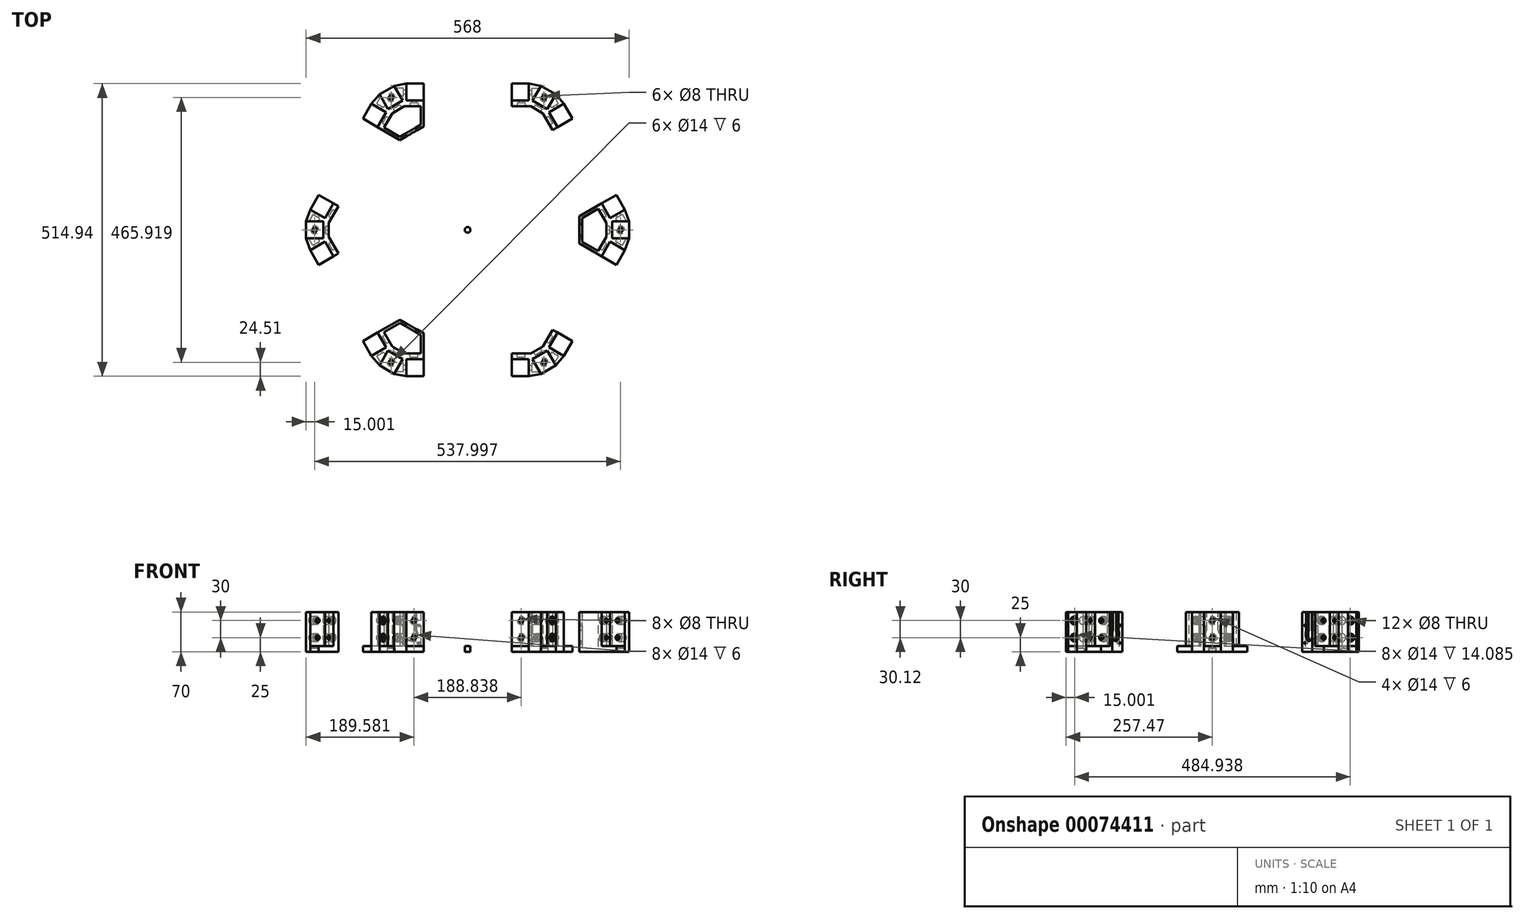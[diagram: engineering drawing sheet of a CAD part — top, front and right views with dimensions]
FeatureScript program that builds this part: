
annotation { "Feature Type Name" : "Feature", "Feature Type Description" : "" }
export const myFeature = defineFeature(function(context is Context, id is Id, definition is map)
    precondition{}
    {
        {
            var Q0;
            Q0=qCreatedBy(makeId("Top.planeOp"),FACE);
            var sketch = newSketch(context, id + "F0", { "sketchPlane" : qUnion([Q0])});
            skCircle(sketch, "E0", {"center": v(0, 0) * mm, "radius": 150 * mm, "construction": true});
            skCircle(sketch, "E1.cCircle", {"center": v(0, 0) * mm, "radius": 253.45 * mm, "construction": true});
            skLineSegment(sketch, "E1.0", {"start": v(-146.33, 253.45) * mm, "end": v(146.33, 253.45) * mm, "construction": true});
            skLineSegment(sketch, "E1.1", {"start": v(146.33, 253.45) * mm, "end": v(292.66, 0) * mm, "construction": true});
            skLineSegment(sketch, "E1.2", {"start": v(292.66, 0) * mm, "end": v(146.33, -253.45) * mm, "construction": true});
            skLineSegment(sketch, "E1.3", {"start": v(146.33, -253.45) * mm, "end": v(-146.33, -253.45) * mm, "construction": true});
            skLineSegment(sketch, "E1.4", {"start": v(-146.33, -253.45) * mm, "end": v(-292.66, 0) * mm, "construction": true});
            skLineSegment(sketch, "E1.5", {"start": v(-292.66, 0) * mm, "end": v(-146.33, 253.45) * mm, "construction": true});
            skPoint(sketch, "E1.0.midPoint", {"position": v(0, 253.45) * mm});
            skLineSegment(sketch, "E2", {"start": v(146.33, 253.45) * mm, "end": v(-146.33, -253.45) * mm, "construction": true});
            skCircle(sketch, "E3.cCircle", {"center": v(0, 0) * mm, "radius": 284 * mm, "construction": true});
            skLineSegment(sketch, "E3.0", {"start": v(0, 327.93) * mm, "end": v(284, 163.97) * mm, "construction": true});
            skLineSegment(sketch, "E3.1", {"start": v(284, 163.97) * mm, "end": v(284, -163.97) * mm, "construction": true});
            skLineSegment(sketch, "E3.2", {"start": v(284, -163.97) * mm, "end": v(0, -327.93) * mm, "construction": true});
            skLineSegment(sketch, "E3.3", {"start": v(0, -327.93) * mm, "end": v(-284, -163.97) * mm, "construction": true});
            skLineSegment(sketch, "E3.4", {"start": v(-284, -163.97) * mm, "end": v(-284, 163.97) * mm, "construction": true});
            skLineSegment(sketch, "E3.5", {"start": v(-284, 163.97) * mm, "end": v(0, 327.93) * mm, "construction": true});
            skPoint(sketch, "E3.0.midPoint", {"position": v(142, 245.95) * mm});
            skLineSegment(sketch, "E4", {"start": v(154.99, 238.45) * mm, "end": v(129, 253.45) * mm});
            skLineSegment(sketch, "E5", {"start": v(-154.99, 238.45) * mm, "end": v(-129, 253.45) * mm});
            skLineSegment(sketch, "E6", {"start": v(-129, 253.45) * mm, "end": v(-114, 227.47) * mm});
            skLineSegment(sketch, "E7", {"start": v(-114, 227.47) * mm, "end": v(-139.99, 212.47) * mm});
            skLineSegment(sketch, "E8", {"start": v(-139.99, 212.47) * mm, "end": v(-154.99, 238.45) * mm});
            skLineSegment(sketch, "E9", {"start": v(129, 253.45) * mm, "end": v(114, 227.47) * mm});
            skLineSegment(sketch, "E10", {"start": v(114, 227.47) * mm, "end": v(139.99, 212.47) * mm});
            skLineSegment(sketch, "E11", {"start": v(139.99, 212.47) * mm, "end": v(154.99, 238.45) * mm});
            skLineSegment(sketch, "E12", {"start": v(284, 15) * mm, "end": v(284, -15) * mm});
            skLineSegment(sketch, "E13", {"start": v(284, -15) * mm, "end": v(254, -15) * mm});
            skLineSegment(sketch, "E14", {"start": v(254, -15) * mm, "end": v(254, 15) * mm});
            skLineSegment(sketch, "E15", {"start": v(254, 15) * mm, "end": v(284, 15) * mm});
            skLineSegment(sketch, "E16", {"start": v(154.99, -238.45) * mm, "end": v(129, -253.45) * mm});
            skLineSegment(sketch, "E17", {"start": v(129, -253.45) * mm, "end": v(114, -227.47) * mm});
            skLineSegment(sketch, "E18", {"start": v(114, -227.47) * mm, "end": v(139.99, -212.47) * mm});
            skLineSegment(sketch, "E19", {"start": v(139.99, -212.47) * mm, "end": v(154.99, -238.45) * mm});
            skLineSegment(sketch, "E20", {"start": v(-129, -253.45) * mm, "end": v(-154.99, -238.45) * mm});
            skLineSegment(sketch, "E21", {"start": v(-154.99, -238.45) * mm, "end": v(-139.99, -212.47) * mm});
            skLineSegment(sketch, "E22", {"start": v(-139.99, -212.47) * mm, "end": v(-114, -227.47) * mm});
            skLineSegment(sketch, "E23", {"start": v(-114, -227.47) * mm, "end": v(-129, -253.45) * mm});
            skLineSegment(sketch, "E24", {"start": v(-284, -15) * mm, "end": v(-284, 15) * mm});
            skLineSegment(sketch, "E25", {"start": v(-284, 15) * mm, "end": v(-254, 15) * mm});
            skLineSegment(sketch, "E26", {"start": v(-254, 15) * mm, "end": v(-254, -15) * mm});
            skLineSegment(sketch, "E27", {"start": v(-254, -15) * mm, "end": v(-284, -15) * mm});
            skLineSegment(sketch, "E28", {"start": v(-254, 15) * mm, "end": v(-139.99, 212.47) * mm, "construction": true});
            skLineSegment(sketch, "E29", {"start": v(-254, -15) * mm, "end": v(-139.99, -212.47) * mm, "construction": true});
            skLineSegment(sketch, "E30", {"start": v(-114, -227.47) * mm, "end": v(114, -227.47) * mm, "construction": true});
            skLineSegment(sketch, "E31", {"start": v(139.99, -212.47) * mm, "end": v(254, -15) * mm, "construction": true});
            skLineSegment(sketch, "E32", {"start": v(254, 15) * mm, "end": v(139.99, 212.47) * mm, "construction": true});
            skLineSegment(sketch, "E33", {"start": v(114, 227.47) * mm, "end": v(-114, 227.47) * mm, "construction": true});
            skLineSegment(sketch, "E34", {"start": v(-114, 227.47) * mm, "end": v(-107.5, 227.47) * mm, "construction": true});
            skLineSegment(sketch, "E35", {"start": v(-107.5, 227.47) * mm, "end": v(-77.5, 227.47) * mm});
            skLineSegment(sketch, "E36", {"start": v(-77.5, 227.47) * mm, "end": v(-77.5, 217.47) * mm});
            skLineSegment(sketch, "E37", {"start": v(-77.5, 217.47) * mm, "end": v(-111.33, 217.47) * mm});
            skLineSegment(sketch, "E38", {"start": v(-111.33, 217.47) * mm, "end": v(-132.67, 205.15) * mm});
            skLineSegment(sketch, "E39", {"start": v(-132.67, 205.15) * mm, "end": v(-149.58, 175.86) * mm});
            skLineSegment(sketch, "E40", {"start": v(-149.58, 175.86) * mm, "end": v(-158.24, 180.86) * mm});
            skLineSegment(sketch, "E41", {"start": v(-158.24, 180.86) * mm, "end": v(-143.24, 206.84) * mm});
            skLineSegment(sketch, "E42", {"start": v(-143.24, 206.84) * mm, "end": v(-139.99, 212.47) * mm, "construction": true});
            skLineSegment(sketch, "E43", {"start": v(-154.99, 238.45) * mm, "end": v(-114, 227.47) * mm, "construction": true});
            skLineSegment(sketch, "E44", {"start": v(-129, 253.45) * mm, "end": v(-139.99, 212.47) * mm, "construction": true});
            skPoint(sketch, "E45", {"position": v(-134.5, 232.96) * mm});
            skCircle(sketch, "E46", {"center": v(0, 0) * mm, "radius": 5 * mm});
            skLineSegment(sketch, "E47", {"start": v(-118.15, 234.63) * mm, "end": v(-118.15, 248.63) * mm, "construction": true});
            skLineSegment(sketch, "E48.0", {"start": v(-112.15, 234.63) * mm, "end": v(-112.15, 248.63) * mm, "construction": true});
            skLineSegment(sketch, "E49.0", {"start": v(-107.5, 257.47) * mm, "end": v(-77.5, 257.47) * mm});
            skLineSegment(sketch, "E50.0", {"start": v(-184.22, 195.86) * mm, "end": v(-169.22, 221.84) * mm});
            skLineSegment(sketch, "E51", {"start": v(-154.99, 238.45) * mm, "end": v(-169.22, 221.84) * mm});
            skLineSegment(sketch, "E52", {"start": v(-107.5, 257.47) * mm, "end": v(-129, 253.45) * mm});
            skLineSegment(sketch, "E53", {"start": v(-107.5, 227.47) * mm, "end": v(-107.5, 257.47) * mm});
            skLineSegment(sketch, "E54", {"start": v(-77.5, 257.47) * mm, "end": v(-77.5, 227.47) * mm});
            skLineSegment(sketch, "E55", {"start": v(-158.24, 180.86) * mm, "end": v(-184.22, 195.86) * mm});
            skLineSegment(sketch, "E56", {"start": v(-143.24, 206.84) * mm, "end": v(-169.22, 221.84) * mm});
            skLineSegment(sketch, "E57", {"start": v(-107.5, 242.47) * mm, "end": v(-122.67, 242.47) * mm, "construction": true});
            skLineSegment(sketch, "E58", {"start": v(-149.58, 175.86) * mm, "end": v(-118.88, 158.14) * mm});
            skLineSegment(sketch, "E59", {"start": v(-118.88, 158.14) * mm, "end": v(-77.5, 182.02) * mm});
            skLineSegment(sketch, "E60", {"start": v(-77.5, 182.02) * mm, "end": v(-77.5, 217.47) * mm});
            skLineSegment(sketch, "E61", {"start": v(-122, 211.3) * mm, "end": v(-98.2, 170.08) * mm, "construction": true});
            skLineSegment(sketch, "E62.1", {"start": v(-118.88, 163.9) * mm, "end": v(-82.5, 184.9) * mm});
            skLineSegment(sketch, "E62.2", {"start": v(-147.08, 180.19) * mm, "end": v(-118.88, 163.9) * mm});
            skLineSegment(sketch, "E63", {"start": v(-82.5, 184.9) * mm, "end": v(-82.5, 217.47) * mm});
            skSolve(sketch);
        }
        {
            var Q0;
            Q0=makeQuery(id+"F0.imprint","IMPRINT",FACE,{"disambiguationData":[TD([[makeQuery(id+"F0.imprint","IMPRINT",EDGE,{"derivedFrom":sQuery(id+"F0.wireOp",EDGE,"E6")}),1.0]])]});
            var Q1;
            Q1=makeQuery(id+"F0.imprint","IMPRINT",FACE,{"disambiguationData":[TD([[makeQuery(id+"F0.imprint","IMPRINT",EDGE,{"derivedFrom":sQuery(id+"F0.wireOp",EDGE,"E25")}),1.0]])]});
            extrude(context, id + "F1", {"entities" : qUnion([Q0, Q1]), "depth" : 70 * mm});
        }
        {
            var Q0;
            Q0=makeQuery(id+"F0.imprint","IMPRINT",FACE,{"disambiguationData":[TD([[makeQuery(id+"F0.imprint","IMPRINT",EDGE,{"derivedFrom":sQuery(id+"F0.wireOp",EDGE,"gfhvg1Dc-7iLy-Ra7s-P4iO-IVNU9nK08UEl")}),-1.0]])]});
            var Q1;
            Q1=makeQuery(id+"F0.imprint","IMPRINT",FACE,{"disambiguationData":[TD([[makeQuery(id+"F0.imprint","IMPRINT",EDGE,{"derivedFrom":sQuery(id+"F0.wireOp",EDGE,"E5")}),-1.0]])]});
            var Q2;
            Q2=makeQuery(id+"F0.imprint","IMPRINT",FACE,{"disambiguationData":[TD([[makeQuery(id+"F0.imprint","IMPRINT",EDGE,{"derivedFrom":sQuery(id+"F0.wireOp",EDGE,"E41")}),1.0]])]});
            var Q3;
            Q3=makeQuery(id+"F0.imprint","IMPRINT",FACE,{"disambiguationData":[TD([[makeQuery(id+"F0.imprint","IMPRINT",EDGE,{"derivedFrom":sQuery(id+"F0.wireOp",EDGE,"kg992uxK-LLUE-ufWO-S31q-0ohrqG9XmHnS")}),1.0]])]});
            var Q4;
            Q4=makeQuery(id+"F0.imprint","IMPRINT",FACE,{"disambiguationData":[TD([[makeQuery(id+"F0.imprint","IMPRINT",EDGE,{"derivedFrom":sQuery(id+"F0.wireOp",EDGE,"zyB05oXD-GM3K-m8Ih-r1cb-nkl0ugIBj9Wl")}),1.0]])]});
            var Q5;
            Q5=makeQuery(id+"F0.imprint","IMPRINT",FACE,{"disambiguationData":[TD([[makeQuery(id+"F0.imprint","IMPRINT",EDGE,{"derivedFrom":sQuery(id+"F0.wireOp",EDGE,"ZcA5kg2R-B5n5-RwAf-hmlT-K68Li3uCES3B")}),-1.0]])]});
            var Q6;
            Q6=makeQuery(id+"F0.imprint","IMPRINT",FACE,{"disambiguationData":[TD([[makeQuery(id+"F0.imprint","IMPRINT",EDGE,{"derivedFrom":sQuery(id+"F0.wireOp",EDGE,"E46")}),1.0]])]});
            var Q7;
            Q7=makeQuery(id+"F0.imprint","IMPRINT",FACE,{"disambiguationData":[TD([[makeQuery(id+"F0.imprint","IMPRINT",EDGE,{"derivedFrom":sQuery(id+"F0.wireOp",EDGE,"E35")}),1.0]])]});
            extrude(context, id + "F2", {"entities" : qUnion([Q0, Q1, Q2, Q3, Q4, Q5, Q6, Q7]), "operationType" : NewBodyOperationType.ADD, "depth" : 10 * mm});
        }
        {
            var Q0;
            Q0=makeQuery(id+"F1.opExtrude","SWEPT_FACE",FACE,{"disambiguationData":[OSD([sQuery(id+"F0.wireOp",EDGE,"E53")])]});
            var Q1;
            Q1=makeQuery(id+"F1.opExtrude","CAP_VERTEX",VERTEX,{"disambiguationData":[OSD([sQuery(id+"F0.wireOp",EDGE,"E5"),sQuery(id+"F0.wireOp",EDGE,"E6"),sQuery(id+"F0.wireOp",EDGE,"E52")])],"isStart":false});
            cPlane(context, id + "F3", {"entities" : qUnion([Q0, Q1]), "cplaneType" : CPlaneType.PLANE_POINT, "offset" : 150 * mm, "width" : 150 * mm, "height" : 150 * mm});
        }
        {
            var Q0;
            Q0=qCreatedBy(id+"F3.planeOp",FACE);
            var sketch = newSketch(context, id + "F4", { "sketchPlane" : qUnion([Q0])});
            skLineSegment(sketch, "E64.0", {"start": v(242.47, 70.12) * mm, "end": v(242.47, 10) * mm, "construction": true});
            skPoint(sketch, "E65", {"position": v(242.47, 55.12) * mm});
            skPoint(sketch, "E66", {"position": v(242.47, 25) * mm});
            skSolve(sketch);
        }
        {
            var Q0;
            Q0=makeQuery(id+"F1.opExtrude","SWEPT_FACE",FACE,{"disambiguationData":[OSD([sQuery(id+"F0.wireOp",EDGE,"E56")])]});
            var Q1;
            Q1=makeQuery(id+"F1.opExtrude","CAP_VERTEX",VERTEX,{"disambiguationData":[OSD([sQuery(id+"F0.wireOp",EDGE,"E5"),sQuery(id+"F0.wireOp",EDGE,"E8"),sQuery(id+"F0.wireOp",EDGE,"E51")])],"isStart":false});
            cPlane(context, id + "F5", {"entities" : qUnion([Q0, Q1]), "cplaneType" : CPlaneType.PLANE_POINT, "offset" : 150 * mm, "width" : 150 * mm, "height" : 150 * mm});
        }
        {
            var Q0;
            Q0=qCreatedBy(id+"F5.planeOp",FACE);
            var sketch = newSketch(context, id + "F6", { "sketchPlane" : qUnion([Q0])});
            skLineSegment(sketch, "E67.0", {"start": v(-242.47, 70) * mm, "end": v(-242.47, 10) * mm, "construction": true});
            skPoint(sketch, "E68", {"position": v(-242.47, 55) * mm});
            skPoint(sketch, "E69", {"position": v(-242.47, 25) * mm});
            skSolve(sketch);
        }
        {
            var Q0;
            Q0=makeQuery(id+"F1.opExtrude","SWEPT_FACE",FACE,{"disambiguationData":[OSD([sQuery(id+"F0.wireOp",EDGE,"E38")])]});
            var sketch = newSketch(context, id + "F7", { "sketchPlane" : qUnion([Q0])});
            skLineSegment(sketch, "E70", {"start": v(0, 70) * mm, "end": v(0, 0) * mm, "construction": true});
            skPoint(sketch, "E71", {"position": v(0, 55) * mm});
            skPoint(sketch, "E72", {"position": v(0, 25) * mm});
            skSolve(sketch);
        }
        {
            var Q0;
            Q0=makeQuery(id+"F1.opExtrude","SWEPT_FACE",FACE,{"disambiguationData":[OSD([sQuery(id+"F0.wireOp",EDGE,"E39")])]});
            var sketch = newSketch(context, id + "F8", { "sketchPlane" : qUnion([Q0])});
            skLineSegment(sketch, "E73", {"start": v(94.42, 70) * mm, "end": v(94.42, 0) * mm, "construction": true});
            skPoint(sketch, "E74", {"position": v(94.42, 55) * mm});
            skPoint(sketch, "E75", {"position": v(94.42, 25) * mm});
            skSolve(sketch);
        }
        {
            var Q0;
            Q0=makeQuery(id+"F1.opExtrude","SWEPT_FACE",FACE,{"disambiguationData":[OSD([sQuery(id+"F0.wireOp",EDGE,"E37")])]});
            var sketch = newSketch(context, id + "F9", { "sketchPlane" : qUnion([Q0])});
            skLineSegment(sketch, "E76", {"start": v(-94.42, 70) * mm, "end": v(-94.42, 0) * mm, "construction": true});
            skPoint(sketch, "E77", {"position": v(-94.42, 55) * mm});
            skPoint(sketch, "E78", {"position": v(-94.42, 25) * mm});
            skSolve(sketch);
        }
        {
            var Q0;
            Q0=sQuery(id+"F4.wireOp",VERTEX,"E65");
            var Q1;
            Q1=sQuery(id+"F4.wireOp",VERTEX,"E66");
            var Q2;
            Q2=sQuery(id+"F0.wireOp",VERTEX,"E45");
            var Q3;
            Q3=sQuery(id+"F6.wireOp",VERTEX,"cff155ce-5f81-47e9-b263-279717c5aa05");
            var Q4;
            Q4=sQuery(id+"F6.wireOp",VERTEX,"238236e4-252f-4cb6-8429-7a6d3b7dbdbb");
            var Q5;
            Q5=sQuery(id+"F6.wireOp",VERTEX,"E68");
            var Q6;
            Q6=sQuery(id+"F6.wireOp",VERTEX,"E69");
            var Q7;
            Q7=makeQuery(id+"F1.opExtrude","SWEPT_BODY",BODY,{"disambiguationData":[OSD([sQuery(id+"F0.wireOp",EDGE,"E6"),sQuery(id+"F0.wireOp",EDGE,"E7"),sQuery(id+"F0.wireOp",EDGE,"E8"),sQuery(id+"F0.wireOp",EDGE,"gfhvg1Dc-7iLy-Ra7s-P4iO-IVNU9nK08UEl"),sQuery(id+"F0.wireOp",EDGE,"2Ei9XriT-fD9c-ETMH-U4qR-QOi2l2HyO4ls"),sQuery(id+"F0.wireOp",EDGE,"E35"),sQuery(id+"F0.wireOp",EDGE,"E36"),sQuery(id+"F0.wireOp",EDGE,"E37"),sQuery(id+"F0.wireOp",EDGE,"E38"),sQuery(id+"F0.wireOp",EDGE,"E39"),sQuery(id+"F0.wireOp",EDGE,"E40"),sQuery(id+"F0.wireOp",EDGE,"E41"),sQuery(id+"F0.wireOp",EDGE,"uSjWHJkC-35aW-f7bu-jVbw-ONZoDCyZtA0Y"),sQuery(id+"F0.wireOp",EDGE,"6PwrACHb-G9Z9-2ubd-gtxy-jkFo4IrFMrrZ")])]});
            hole(context, id + "F10", {"style" : HoleStyle.C_BORE, "holeDiameter" : 8 * mm, "cBoreDiameter" : 14 * mm, "cBoreDepth" : 6 * mm, "endStyle" : HoleEndStyle.BLIND, "oppositeDirection" : true, "holeDepth" : 20 * mm, "locations" : qUnion([Q0, Q1, Q2, Q3, Q4, Q5, Q6]), "scope" : qUnion([Q7])});
        }
        {
            var Q0;
            Q0=sQuery(id+"F9.wireOp",VERTEX,"E77");
            var Q1;
            Q1=sQuery(id+"F9.wireOp",VERTEX,"E78");
            var Q2;
            Q2=sQuery(id+"F7.wireOp",VERTEX,"E71");
            var Q3;
            Q3=sQuery(id+"F7.wireOp",VERTEX,"E72");
            var Q4;
            Q4=sQuery(id+"F8.wireOp",VERTEX,"E75");
            var Q5;
            Q5=sQuery(id+"F8.wireOp",VERTEX,"E74");
            var Q6;
            Q6=makeQuery(id+"F1.opExtrude","SWEPT_BODY",BODY,{"disambiguationData":[OSD([sQuery(id+"F0.wireOp",EDGE,"E6"),sQuery(id+"F0.wireOp",EDGE,"E7"),sQuery(id+"F0.wireOp",EDGE,"E8"),sQuery(id+"F0.wireOp",EDGE,"gfhvg1Dc-7iLy-Ra7s-P4iO-IVNU9nK08UEl"),sQuery(id+"F0.wireOp",EDGE,"2Ei9XriT-fD9c-ETMH-U4qR-QOi2l2HyO4ls"),sQuery(id+"F0.wireOp",EDGE,"E35"),sQuery(id+"F0.wireOp",EDGE,"E36"),sQuery(id+"F0.wireOp",EDGE,"E37"),sQuery(id+"F0.wireOp",EDGE,"E38"),sQuery(id+"F0.wireOp",EDGE,"E39"),sQuery(id+"F0.wireOp",EDGE,"E40"),sQuery(id+"F0.wireOp",EDGE,"E41"),sQuery(id+"F0.wireOp",EDGE,"uSjWHJkC-35aW-f7bu-jVbw-ONZoDCyZtA0Y"),sQuery(id+"F0.wireOp",EDGE,"6PwrACHb-G9Z9-2ubd-gtxy-jkFo4IrFMrrZ")])]});
            hole(context, id + "F11", {"style" : HoleStyle.C_BORE, "holeDiameter" : 8 * mm, "cBoreDiameter" : 14 * mm, "cBoreDepth" : 6 * mm, "endStyle" : HoleEndStyle.THROUGH, "locations" : qUnion([Q0, Q1, Q2, Q3, Q4, Q5]), "scope" : qUnion([Q6])});
        }
        {
            var Q0;
            Q0=makeQuery(id+"F1.opExtrude","SWEPT_BODY",BODY,{"disambiguationData":[OSD([sQuery(id+"F0.wireOp",EDGE,"E6"),sQuery(id+"F0.wireOp",EDGE,"E7"),sQuery(id+"F0.wireOp",EDGE,"E8"),sQuery(id+"F0.wireOp",EDGE,"gfhvg1Dc-7iLy-Ra7s-P4iO-IVNU9nK08UEl"),sQuery(id+"F0.wireOp",EDGE,"2Ei9XriT-fD9c-ETMH-U4qR-QOi2l2HyO4ls"),sQuery(id+"F0.wireOp",EDGE,"E35"),sQuery(id+"F0.wireOp",EDGE,"E36"),sQuery(id+"F0.wireOp",EDGE,"E37"),sQuery(id+"F0.wireOp",EDGE,"E38"),sQuery(id+"F0.wireOp",EDGE,"E39"),sQuery(id+"F0.wireOp",EDGE,"E40"),sQuery(id+"F0.wireOp",EDGE,"E41"),sQuery(id+"F0.wireOp",EDGE,"uSjWHJkC-35aW-f7bu-jVbw-ONZoDCyZtA0Y"),sQuery(id+"F0.wireOp",EDGE,"6PwrACHb-G9Z9-2ubd-gtxy-jkFo4IrFMrrZ")])]});
            var Q1;
            Q1=sQuery(id+"F0.wireOp",EDGE,"E3.cCircle");
            circularPattern(context, id + "F12", {"entities" : qUnion([Q0]), "axis" : qUnion([Q1]), "angle" : 60 * degree, "instanceCount" : round(2)});
        }
        {
            var Q0;
            {var subQ0=sQuery(id+"F0.wireOp",EDGE,"E58");Q0=makeQuery(id+"F0.imprint","IMPRINT",FACE,{"disambiguationData":[TD([[makeQuery(id+"F0.imprint","IMPRINT",EDGE,{"derivedFrom":subQ0}),1.0]])]});}
            extrude(context, id + "F13", {"entities" : qUnion([Q0]), "operationType" : NewBodyOperationType.ADD, "depth" : 70 * mm});
        }
        {
            var Q0;
            Q0=makeQuery(id+"F13.opExtrude","SWEPT_FACE",FACE,{"disambiguationData":[OSD([sQuery(id+"F0.wireOp",EDGE,"E59")])]});
            var sketch = newSketch(context, id + "F14", { "sketchPlane" : qUnion([Q0])});
            skLineSegment(sketch, "E79.0", {"start": v(-23.89, 10) * mm, "end": v(23.89, 10) * mm, "construction": true});
            skLineSegment(sketch, "E80.0", {"start": v(-23.89, 52) * mm, "end": v(23.89, 52) * mm, "construction": true});
            skLineSegment(sketch, "E81.0", {"start": v(-23.89, 46.5) * mm, "end": v(23.89, 46.5) * mm, "construction": true});
            skLineSegment(sketch, "E82.0", {"start": v(-23.89, 15.5) * mm, "end": v(23.89, 15.5) * mm, "construction": true});
            skPoint(sketch, "E83", {"position": v(0, 31) * mm});
            skLineSegment(sketch, "E84", {"start": v(0, 70) * mm, "end": v(0, 0) * mm, "construction": true});
            skLineSegment(sketch, "E85.0", {"start": v(-15.5, 70) * mm, "end": v(-15.5, 0) * mm, "construction": true});
            skLineSegment(sketch, "E86.0", {"start": v(15.5, 70) * mm, "end": v(15.5, 0) * mm, "construction": true});
            skLineSegment(sketch, "E87", {"start": v(15.5, 15.5) * mm, "end": v(-15.5, 46.5) * mm, "construction": true});
            skLineSegment(sketch, "E88", {"start": v(15.5, 46.5) * mm, "end": v(-15.5, 15.5) * mm, "construction": true});
            skCircle(sketch, "E89", {"center": v(0, 31) * mm, "radius": 12 * mm});
            skLineSegment(sketch, "E90.0", {"start": v(-10, 70) * mm, "end": v(-10, 0) * mm, "construction": true});
            skLineSegment(sketch, "E91.0", {"start": v(10, 70) * mm, "end": v(10, 0) * mm, "construction": true});
            skLineSegment(sketch, "E92", {"start": v(-10, 37.63) * mm, "end": v(-10, 70) * mm});
            skLineSegment(sketch, "E93", {"start": v(10, 37.63) * mm, "end": v(10, 70) * mm});
            skSolve(sketch);
        }
        {
            var Q0;
            Q0=qSketchRegion(id+"F14",true);
            var Q1;
            {var subQ0=sQuery(id+"F14.wireOp",EDGE,"E92");Q1=makeQuery(id+"F14.imprint","IMPRINT",FACE,{"disambiguationData":[TD([[makeQuery(id+"F14.imprint","IMPRINT",EDGE,{"derivedFrom":subQ0}),-1.0]])]});}
            extrude(context, id + "F15", {"entities" : qUnion([Q0, Q1]), "operationType" : NewBodyOperationType.REMOVE, "oppositeDirection" : true, "depth" : 5 * mm});
        }
        {
            var Q0;
            Q0=sQuery(id+"F14.wireOp",VERTEX,"E87.end");
            var Q1;
            Q1=sQuery(id+"F14.wireOp",VERTEX,"E88.start");
            var Q2;
            Q2=sQuery(id+"F14.wireOp",VERTEX,"E87.start");
            var Q3;
            Q3=sQuery(id+"F14.wireOp",VERTEX,"E88.end");
            var Q4;
            Q4=makeQuery(id+"F1.opExtrude","SWEPT_BODY",BODY,{"disambiguationData":[OSD([sQuery(id+"F0.wireOp",EDGE,"E6"),sQuery(id+"F0.wireOp",EDGE,"E7"),sQuery(id+"F0.wireOp",EDGE,"E8"),sQuery(id+"F0.wireOp",EDGE,"E35"),sQuery(id+"F0.wireOp",EDGE,"E36"),sQuery(id+"F0.wireOp",EDGE,"E37"),sQuery(id+"F0.wireOp",EDGE,"E38"),sQuery(id+"F0.wireOp",EDGE,"E39"),sQuery(id+"F0.wireOp",EDGE,"E40"),sQuery(id+"F0.wireOp",EDGE,"E41"),sQuery(id+"F0.wireOp",EDGE,"E51"),sQuery(id+"F0.wireOp",EDGE,"E52"),sQuery(id+"F0.wireOp",EDGE,"E53"),sQuery(id+"F0.wireOp",EDGE,"E56")])]});
            hole(context, id + "F16", {"style" : HoleStyle.SIMPLE, "holeDiameter" : 3 * mm, "endStyle" : HoleEndStyle.BLIND, "holeDepth" : 20 * mm, "locations" : qUnion([Q0, Q1, Q2, Q3]), "scope" : qUnion([Q4])});
        }
        {
            var Q0;
            Q0=makeQuery(id+"F1.opExtrude","SWEPT_BODY",BODY,{"disambiguationData":[OSD([sQuery(id+"F0.wireOp",EDGE,"E6"),sQuery(id+"F0.wireOp",EDGE,"E7"),sQuery(id+"F0.wireOp",EDGE,"E8"),sQuery(id+"F0.wireOp",EDGE,"gfhvg1Dc-7iLy-Ra7s-P4iO-IVNU9nK08UEl"),sQuery(id+"F0.wireOp",EDGE,"2Ei9XriT-fD9c-ETMH-U4qR-QOi2l2HyO4ls"),sQuery(id+"F0.wireOp",EDGE,"E35"),sQuery(id+"F0.wireOp",EDGE,"E36"),sQuery(id+"F0.wireOp",EDGE,"E37"),sQuery(id+"F0.wireOp",EDGE,"E38"),sQuery(id+"F0.wireOp",EDGE,"E39"),sQuery(id+"F0.wireOp",EDGE,"E40"),sQuery(id+"F0.wireOp",EDGE,"E41"),sQuery(id+"F0.wireOp",EDGE,"uSjWHJkC-35aW-f7bu-jVbw-ONZoDCyZtA0Y"),sQuery(id+"F0.wireOp",EDGE,"6PwrACHb-G9Z9-2ubd-gtxy-jkFo4IrFMrrZ")])]});
            var Q1;
            Q1=sQuery(id+"F0.wireOp",EDGE,"E3.cCircle");
            circularPattern(context, id + "F17", {"entities" : qUnion([Q0]), "axis" : qUnion([Q1]), "angle" : 120 * degree, "instanceCount" : round(3)});
        }
        {
            var Q0;
            Q0=makeQuery(id+"F12.opPattern","COPY",BODY,{"derivedFrom":makeQuery(id+"F1.opExtrude","SWEPT_BODY",BODY,{"disambiguationData":[OSD([sQuery(id+"F0.wireOp",EDGE,"E6"),sQuery(id+"F0.wireOp",EDGE,"E7"),sQuery(id+"F0.wireOp",EDGE,"E8"),sQuery(id+"F0.wireOp",EDGE,"gfhvg1Dc-7iLy-Ra7s-P4iO-IVNU9nK08UEl"),sQuery(id+"F0.wireOp",EDGE,"2Ei9XriT-fD9c-ETMH-U4qR-QOi2l2HyO4ls"),sQuery(id+"F0.wireOp",EDGE,"E35"),sQuery(id+"F0.wireOp",EDGE,"E36"),sQuery(id+"F0.wireOp",EDGE,"E37"),sQuery(id+"F0.wireOp",EDGE,"E38"),sQuery(id+"F0.wireOp",EDGE,"E39"),sQuery(id+"F0.wireOp",EDGE,"E40"),sQuery(id+"F0.wireOp",EDGE,"E41"),sQuery(id+"F0.wireOp",EDGE,"uSjWHJkC-35aW-f7bu-jVbw-ONZoDCyZtA0Y"),sQuery(id+"F0.wireOp",EDGE,"6PwrACHb-G9Z9-2ubd-gtxy-jkFo4IrFMrrZ")])]}),"instanceName":"1"});
            var Q1;
            Q1=sQuery(id+"F0.wireOp",EDGE,"E3.cCircle");
            circularPattern(context, id + "F18", {"entities" : qUnion([Q0]), "axis" : qUnion([Q1]), "angle" : 120 * degree, "instanceCount" : round(3)});
        }
        {
            var Q0;
            Q0=makeQuery(id+"F15.boolean.opBoolean","COPY",EDGE,{"derivedFrom":makeQuery(id+"F15.opExtrude","SWEPT_EDGE",EDGE,{"disambiguationData":[OSD([sQuery(id+"F0.wireOp",EDGE,"E59"),sQuery(id+"F14.wireOp",EDGE,"E92")])]})});
            var Q1;
            Q1=makeQuery(id+"F15.boolean.opBoolean","COPY",EDGE,{"derivedFrom":makeQuery(id+"F15.opExtrude","SWEPT_EDGE",EDGE,{"disambiguationData":[OSD([sQuery(id+"F0.wireOp",EDGE,"E59"),sQuery(id+"F14.wireOp",EDGE,"E93")])]})});
            var Q2;
            Q2=makeQuery(id+"F15.boolean.opBoolean","COPY",EDGE,{"derivedFrom":makeQuery(id+"F15.opExtrude","SWEPT_EDGE",EDGE,{"disambiguationData":[OSD([sQuery(id+"F14.wireOp",EDGE,"E89"),sQuery(id+"F14.wireOp",EDGE,"E92")])]})});
            var Q3;
            Q3=makeQuery(id+"F15.boolean.opBoolean","COPY",EDGE,{"derivedFrom":makeQuery(id+"F15.opExtrude","SWEPT_EDGE",EDGE,{"disambiguationData":[OSD([sQuery(id+"F14.wireOp",EDGE,"E89"),sQuery(id+"F14.wireOp",EDGE,"E93")])]})});
            fillet(context, id + "F19", {"entities" : qUnion([Q0, Q1, Q2, Q3]), "radius" : 10 * mm, "tangentPropagation" : true, "allowEdgeOverflow" : false});
        }
    });
